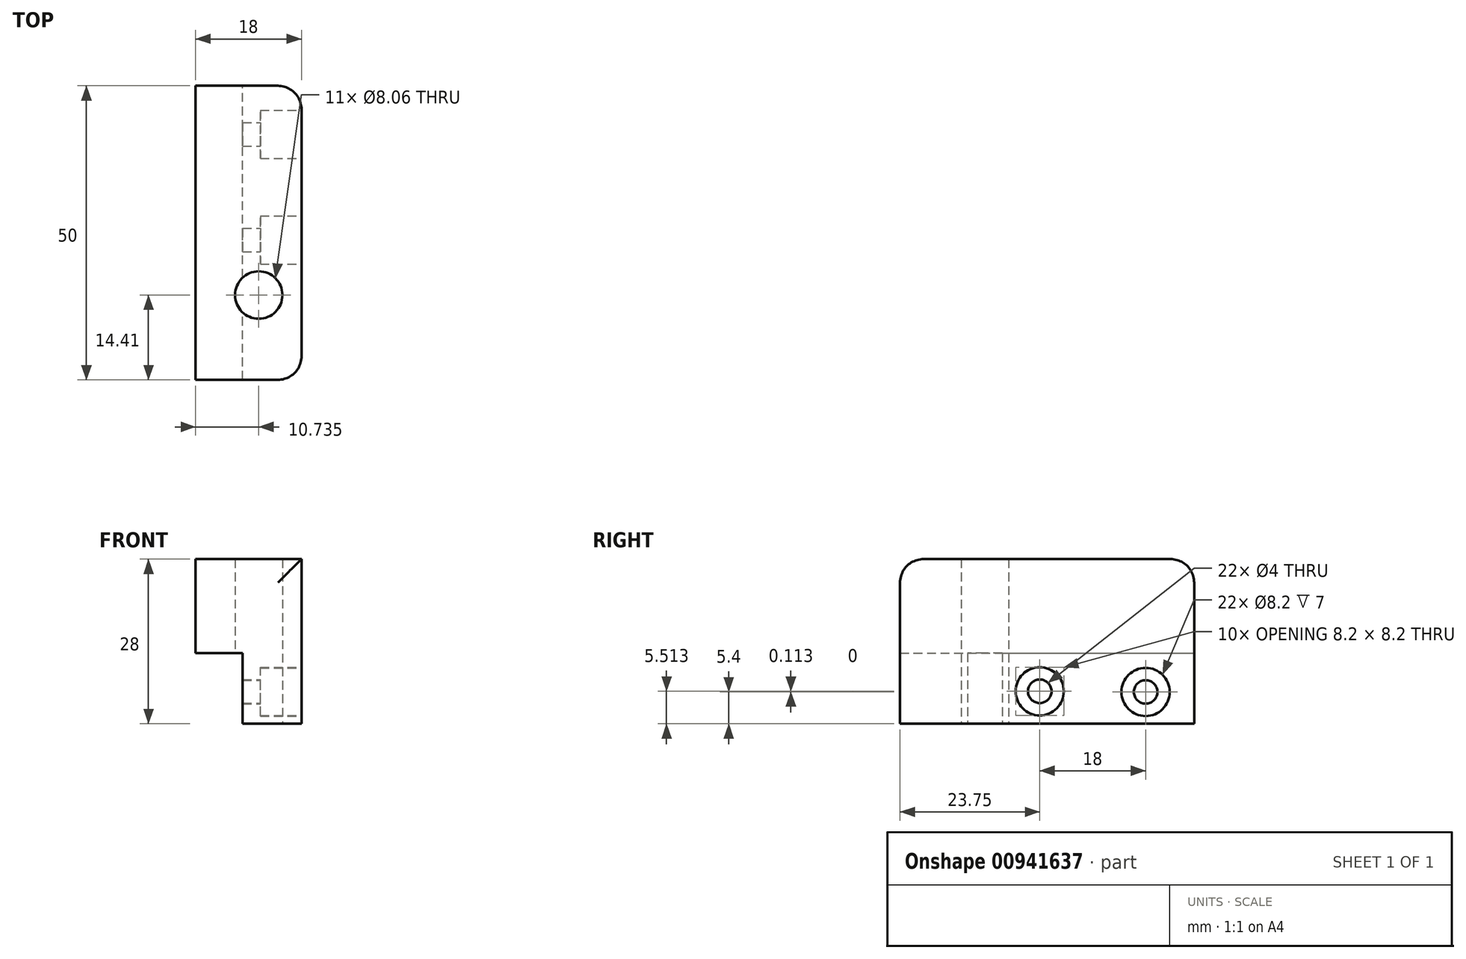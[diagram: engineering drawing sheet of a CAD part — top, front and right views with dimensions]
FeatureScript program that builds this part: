
annotation { "Feature Type Name" : "Feature", "Feature Type Description" : "" }
export const myFeature = defineFeature(function(context is Context, id is Id, definition is map)
    precondition{}
    {
        {
            var Q0;
            Q0=qCreatedBy(makeId("Front.planeOp"),FACE);
            var sketch = newSketch(context, id + "F0", { "sketchPlane" : qUnion([Q0])});
            skLineSegment(sketch, "E0", {"start": v(0, 0) * mm, "end": v(10, 0) * mm});
            skLineSegment(sketch, "E1", {"start": v(10, 0) * mm, "end": v(10, 28) * mm});
            skLineSegment(sketch, "E2", {"start": v(10, 28) * mm, "end": v(-8, 28) * mm});
            skLineSegment(sketch, "E3", {"start": v(-8, 28) * mm, "end": v(-8, 12) * mm});
            skLineSegment(sketch, "E4", {"start": v(-8, 12) * mm, "end": v(0, 12) * mm});
            skLineSegment(sketch, "E5", {"start": v(0, 12) * mm, "end": v(0, 0) * mm});
            skSolve(sketch);
        }
        {
            var Q0;
            Q0=makeQuery(id+"F0.imprint","IMPRINT",FACE,{"disambiguationData":[TD([[makeQuery(id+"F0.imprint","IMPRINT",EDGE,{"derivedFrom":sQuery(id+"F0.wireOp",EDGE,"E0")}),1.0]])]});
            extrude(context, id + "F1", {"entities" : qUnion([Q0]), "depth" : 50 * mm, "offsetDistance" : 25 * mm});
        }
        {
            var Q0;
            Q0=makeQuery(id+"F1.opExtrude","SWEPT_FACE",FACE,{"disambiguationData":[OSD([sQuery(id+"F0.wireOp",EDGE,"E1")])]});
            var sketch = newSketch(context, id + "F2", { "sketchPlane" : qUnion([Q0])});
            skCircle(sketch, "E6", {"center": v(-8.25, 5.4) * mm, "radius": 2 * mm});
            skCircle(sketch, "E7", {"center": v(-26.25, 5.51) * mm, "radius": 2 * mm});
            skCircle(sketch, "E8", {"center": v(-26.25, 5.51) * mm, "radius": 4.1 * mm});
            skCircle(sketch, "E9", {"center": v(-8.25, 5.4) * mm, "radius": 4.1 * mm});
            skSolve(sketch);
        }
        {
            var Q0;
            Q0=makeQuery(id+"F2.imprint","IMPRINT",FACE,{"disambiguationData":[TD([[makeQuery(id+"F2.imprint","IMPRINT",EDGE,{"derivedFrom":sQuery(id+"F2.wireOp",EDGE,"E7")}),1.0]])]});
            var Q1;
            Q1=makeQuery(id+"F2.imprint","IMPRINT",FACE,{"disambiguationData":[TD([[makeQuery(id+"F2.imprint","IMPRINT",EDGE,{"derivedFrom":sQuery(id+"F2.wireOp",EDGE,"E6")}),1.0]])]});
            extrude(context, id + "F3", {"entities" : qUnion([Q0, Q1]), "operationType" : NewBodyOperationType.REMOVE, "oppositeDirection" : true, "depth" : 25 * mm, "offsetDistance" : 25 * mm});
        }
        {
            var Q0;
            Q0=qCreatedBy(makeId("Top.planeOp"),FACE);
            var sketch = newSketch(context, id + "F4", { "sketchPlane" : qUnion([Q0])});
            skCircle(sketch, "E10", {"center": v(2.74, -35.6) * mm, "radius": 4.03 * mm});
            skLineSegment(sketch, "E11", {"start": v(-2.72, -23.6) * mm, "end": v(12.7, -23.6) * mm});
            skSolve(sketch);
        }
        {
            var Q0;
            Q0=makeQuery(id+"F4.imprint","IMPRINT",FACE,{"disambiguationData":[TD([[makeQuery(id+"F4.imprint","IMPRINT",EDGE,{"derivedFrom":sQuery(id+"F4.wireOp",EDGE,"E10")}),1.0]])]});
            var Q1;
            Q1=sQuery(id+"F4.wireOp",EDGE,"E10");
            extrude(context, id + "F5", {"entities" : qUnion([Q0]), "operationType" : NewBodyOperationType.REMOVE, "surfaceEntities" : qUnion([Q1]), "depth" : 28.8 * mm, "offsetDistance" : 25 * mm, "hasSecondDirection" : true, "secondDirectionOppositeDirection" : true, "secondDirectionDepth" : 25 * mm});
        }
        {
            var Q0;
            Q0 = qSketchRegion(id + "F2", true);
            extrude(context, id + "F6", {"entities" : qUnion([Q0]), "operationType" : NewBodyOperationType.REMOVE, "endBound" : BoundingType.SYMMETRIC, "oppositeDirection" : true, "depth" : 14 * mm, "offsetDistance" : 25 * mm});
        }
        {
            var Q0;
            Q0=makeQuery(id+"F1.opExtrude","CAP_EDGE",EDGE,{"disambiguationData":[OSD([sQuery(id+"F0.wireOp",EDGE,"E2")])],"isStart":false});
            var Q1;
            Q1=makeQuery(id+"F1.opExtrude","CAP_EDGE",EDGE,{"disambiguationData":[OSD([sQuery(id+"F0.wireOp",EDGE,"E2")])],"isStart":true});
            var Q2;
            Q2=makeQuery(id+"F1.opExtrude","CAP_EDGE",EDGE,{"disambiguationData":[OSD([sQuery(id+"F0.wireOp",EDGE,"E1")])],"isStart":false});
            var Q3;
            Q3=makeQuery(id+"F1.opExtrude","CAP_EDGE",EDGE,{"disambiguationData":[OSD([sQuery(id+"F0.wireOp",EDGE,"E1")])],"isStart":true});
            fillet(context, id + "F7", {"entities" : qUnion([Q0, Q1, Q2, Q3]), "radius" : 4 * mm, "tangentPropagation" : true, "allowEdgeOverflow" : false});
        }
    });
